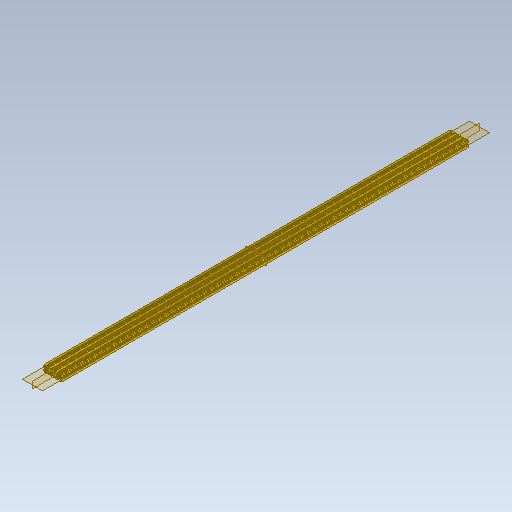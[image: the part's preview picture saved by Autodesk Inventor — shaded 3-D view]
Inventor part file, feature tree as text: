
AUTODESK INVENTOR PART (.ipt)
format: ipt  version: 2025.2 (Build 292293000, 293)  size: 579,584 bytes
history: native  units: mm
features: mirror x6, sketch x2, extrude x2
ambient origin geometry x8: Origin, YZ Plane, XZ Plane, XY Plane, X Axis, Y Axis, Z Axis, Center Point
bodies: Body1 (feature_tree)
feature tree (10):
  sketch  "Esboço1"  dims[d0=15.0mm d1=90.0mm]
  extrude  "Extrusão4"  Depth=90.0mm
  mirror  "Espelhar5"
  mirror  "Espelhar6"
  mirror  "Espelhar7"
  extrude  "Extrusão3"  Depth=8.2mm
  mirror  "Espelhar8"
  mirror  "Espelhar9"
  mirror  "Espelhar10"
  sketch  "Esboço - Padrão circular1"  dims[d4=10.0mm d6=8.2mm d7=15.0mm d11=0.5mm d12=1.1mm d13=8.0mm d14=11.5mm d15=4.5mm d16=1.1mm d17=1.1mm d18=2.0mm d19=1.1mm d20=2.2mm d25=30.0mm d26=2000.0mm d27=0.0mm d28=2000.0mm d29=0.0mm d30=2.2mm d31=20.0mm d33=90.0deg]
